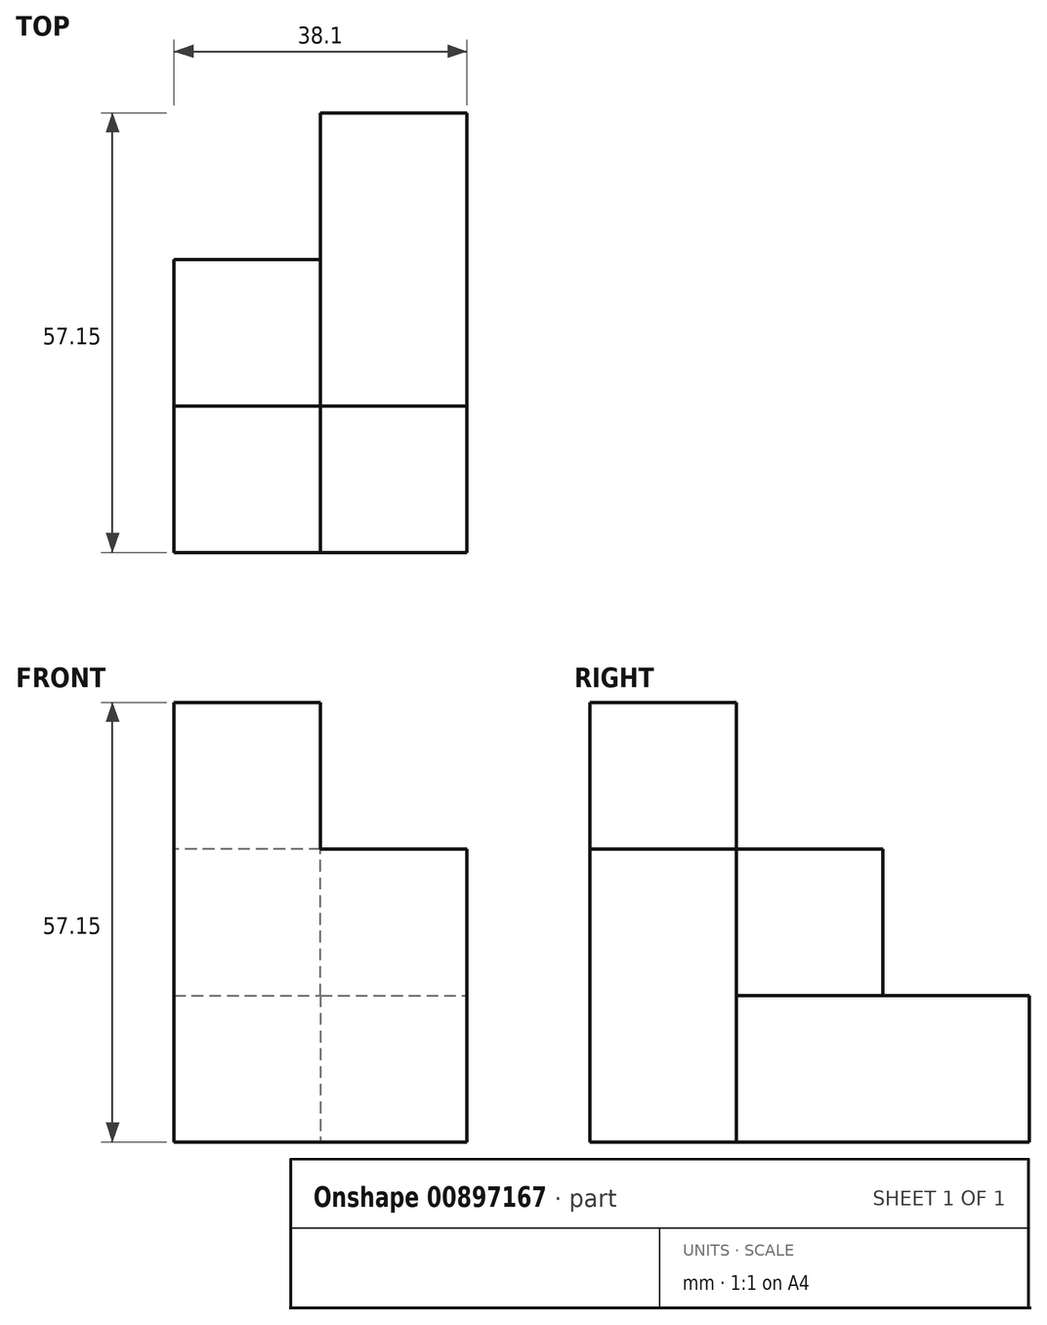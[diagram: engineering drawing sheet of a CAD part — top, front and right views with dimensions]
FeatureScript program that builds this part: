
annotation { "Feature Type Name" : "Feature", "Feature Type Description" : "" }
export const myFeature = defineFeature(function(context is Context, id is Id, definition is map)
    precondition{}
    {
        {
            var Q0;
            Q0=qCreatedBy(makeId("Front.planeOp"),FACE);
            var sketch = newSketch(context, id + "F0", { "sketchPlane" : qUnion([Q0])});
            skLineSegment(sketch, "E0", {"start": v(0, 0) * mm, "end": v(19.05, 0) * mm});
            skLineSegment(sketch, "E1", {"start": v(19.05, 0) * mm, "end": v(19.05, 19.05) * mm});
            skLineSegment(sketch, "E2", {"start": v(19.05, 19.05) * mm, "end": v(0, 19.05) * mm});
            skLineSegment(sketch, "E3", {"start": v(0, 19.05) * mm, "end": v(0, 0) * mm});
            skLineSegment(sketch, "E4", {"start": v(19.05, 19.05) * mm, "end": v(19.05, 38.1) * mm});
            skLineSegment(sketch, "E5", {"start": v(19.05, 38.1) * mm, "end": v(0, 38.1) * mm});
            skLineSegment(sketch, "E6", {"start": v(0, 19.05) * mm, "end": v(0, 38.1) * mm});
            skLineSegment(sketch, "E7", {"start": v(19.05, 0) * mm, "end": v(38.1, 0) * mm});
            skLineSegment(sketch, "E8", {"start": v(38.1, 0) * mm, "end": v(38.1, 19.05) * mm});
            skLineSegment(sketch, "E9", {"start": v(38.1, 19.05) * mm, "end": v(19.05, 19.05) * mm});
            skLineSegment(sketch, "E10", {"start": v(0, 0) * mm, "end": v(0, -19.05) * mm});
            skLineSegment(sketch, "E11", {"start": v(0, -19.05) * mm, "end": v(19.05, -19.05) * mm});
            skLineSegment(sketch, "E12", {"start": v(19.05, -19.05) * mm, "end": v(19.05, 0) * mm});
            skLineSegment(sketch, "E13", {"start": v(19.05, -19.05) * mm, "end": v(38.1, -19.05) * mm});
            skLineSegment(sketch, "E14", {"start": v(38.1, -19.05) * mm, "end": v(38.1, 0) * mm});
            skSolve(sketch);
        }
        {
            var Q0;
            Q0 = qSketchRegion(id + "F0", true);
            extrude(context, id + "F1", {"entities" : qUnion([Q0]), "depth" : 19.05 * mm, "offsetDistance" : 25.4 * mm});
        }
        {
            var Q0;
            Q0=makeQuery(id+"F1.opExtrude","CAP_FACE",FACE,{"disambiguationData":[OSD([sQuery(id+"F0.wireOp",EDGE,"E3"),sQuery(id+"F0.wireOp",EDGE,"E4"),sQuery(id+"F0.wireOp",EDGE,"E5"),sQuery(id+"F0.wireOp",EDGE,"E6"),sQuery(id+"F0.wireOp",EDGE,"E8"),sQuery(id+"F0.wireOp",EDGE,"E9"),sQuery(id+"F0.wireOp",EDGE,"E10"),sQuery(id+"F0.wireOp",EDGE,"E11"),sQuery(id+"F0.wireOp",EDGE,"E13"),sQuery(id+"F0.wireOp",EDGE,"E14")])],"isStart":true});
            var sketch = newSketch(context, id + "F2", { "sketchPlane" : qUnion([Q0])});
            skLineSegment(sketch, "E15", {"start": v(-19.05, 19.05) * mm, "end": v(0, 19.05) * mm});
            skLineSegment(sketch, "E16", {"start": v(0, 19.05) * mm, "end": v(0, 0) * mm});
            skLineSegment(sketch, "E17", {"start": v(0, 0) * mm, "end": v(-19.05, 0) * mm});
            skLineSegment(sketch, "E18", {"start": v(-19.05, 0) * mm, "end": v(-19.05, 19.05) * mm});
            skSolve(sketch);
        }
        {
            var Q0;
            Q0 = qSketchRegion(id + "F2", true);
            extrude(context, id + "F3", {"entities" : qUnion([Q0]), "operationType" : NewBodyOperationType.ADD, "depth" : 19.05 * mm, "offsetDistance" : 25.4 * mm});
        }
        {
            var Q0;
            Q0=qCreatedBy(makeId("Front.planeOp"),FACE);
            var sketch = newSketch(context, id + "F4", { "sketchPlane" : qUnion([Q0])});
            skLineSegment(sketch, "E19", {"start": v(38.28, 0) * mm, "end": v(57.33, 0) * mm});
            skLineSegment(sketch, "E20", {"start": v(57.33, 0) * mm, "end": v(57.33, -19.05) * mm});
            skLineSegment(sketch, "E21", {"start": v(57.33, -19.05) * mm, "end": v(38.28, -19.05) * mm});
            skLineSegment(sketch, "E22", {"start": v(38.28, 0) * mm, "end": v(38.28, -19.05) * mm});
            skSolve(sketch);
        }
        {
            var Q0;
            Q0 = qSketchRegion(id + "F4", true);
            extrude(context, id + "F5", {"entities" : qUnion([Q0]), "depth" : -38.1 * mm, "offsetDistance" : 25.4 * mm});
        }
        {
            var Q0;
            Q0=makeQuery(id+"F5.opExtrude","SWEPT_BODY",BODY,{"disambiguationData":[OSD([sQuery(id+"F4.wireOp",EDGE,"E19"),sQuery(id+"F4.wireOp",EDGE,"E20"),sQuery(id+"F4.wireOp",EDGE,"E21"),sQuery(id+"F4.wireOp",EDGE,"E22")])]});
            transform(context, id + "F6", {"entities" : qUnion([Q0]), "transformType" : TransformType.TRANSLATION_3D, "dx" : -19.23 * mm, "dy" : 0 * mm, "dz" : 0 * mm, "makeCopy" : false});
        }
    });
